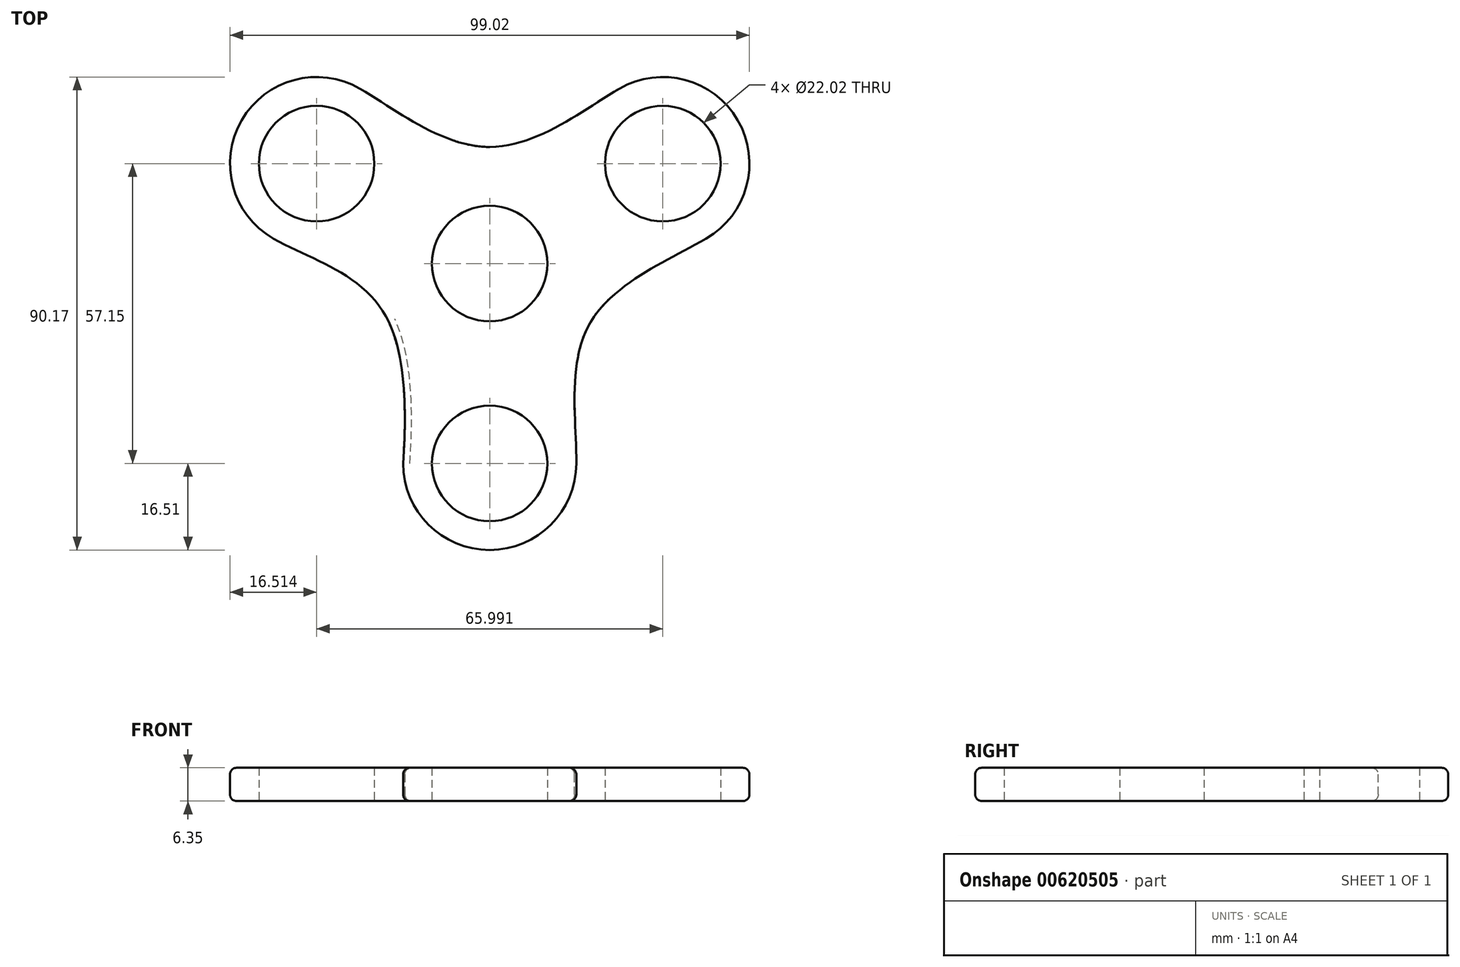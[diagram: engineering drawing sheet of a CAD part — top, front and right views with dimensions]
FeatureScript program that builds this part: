
annotation { "Feature Type Name" : "Feature", "Feature Type Description" : "" }
export const myFeature = defineFeature(function(context is Context, id is Id, definition is map)
    precondition{}
    {
        {
            var Q0;
            Q0=qCreatedBy(makeId("Top.planeOp"),FACE);
            var sketch = newSketch(context, id + "F0", { "sketchPlane" : qUnion([Q0])});
            skCircle(sketch, "E0", {"center": v(0, 0) * mm, "radius": 11.01 * mm});
            skCircle(sketch, "E1", {"center": v(-33, 19.05) * mm, "radius": 11.01 * mm});
            skCircle(sketch, "E2", {"center": v(0, -38.1) * mm, "radius": 11.01 * mm});
            skCircle(sketch, "E3", {"center": v(33, 19.05) * mm, "radius": 11.01 * mm});
            skLineSegment(sketch, "E4", {"start": v(0, 0) * mm, "end": v(-33, 19.05) * mm});
            skLineSegment(sketch, "E5", {"start": v(0, 0) * mm, "end": v(0, -38.1) * mm});
            skLineSegment(sketch, "E6", {"start": v(0, 0) * mm, "end": v(33, 19.05) * mm});
            skCircle(sketch, "E7", {"center": v(-33, 19.05) * mm, "radius": 16.51 * mm});
            skCircle(sketch, "E8", {"center": v(33, 19.05) * mm, "radius": 16.51 * mm});
            skCircle(sketch, "E9", {"center": v(0, -38.1) * mm, "radius": 16.51 * mm});
            skFitSpline(sketch, "E10", {"points": [v(-24.74, 33.35) * mm, v(0, 22.23) * mm, v(24.74, 33.35) * mm], "startDerivative": vector(38.46, -22.2) * mm, "endDerivative": vector(38.2, 22.05) * mm});
            skFitSpline(sketch, "E11", {"points": [v(41.25, 4.75) * mm, v(19.25, -11.11) * mm, v(16.51, -38.1) * mm], "startDerivative": vector(-40.53, -23.4) * mm, "endDerivative": vector(0, -52.53) * mm});
            skFitSpline(sketch, "E12", {"points": [v(-41.25, 4.75) * mm, v(-19.25, -11.11) * mm, v(-16.51, -38.1) * mm], "startDerivative": vector(40.94, -23.64) * mm, "endDerivative": vector(0, -7.4) * mm});
            skCircle(sketch, "E13", {"center": v(0, 0) * mm, "radius": 16.55 * mm});
            skLineSegment(sketch, "E14", {"start": v(0, 0) * mm, "end": v(-19.25, -11.11) * mm});
            skLineSegment(sketch, "E15", {"start": v(0, 0) * mm, "end": v(0, 22.22) * mm});
            skLineSegment(sketch, "E16", {"start": v(0, 0) * mm, "end": v(19.25, -11.11) * mm});
            skLineSegment(sketch, "E17", {"start": v(-33, 19.05) * mm, "end": v(-13.26, 53.24) * mm});
            skLineSegment(sketch, "E18", {"start": v(-13.26, 53.24) * mm, "end": v(-33, 19.05) * mm});
            skLineSegment(sketch, "E19", {"start": v(-33, 19.05) * mm, "end": v(-51.08, -12.28) * mm});
            skLineSegment(sketch, "E20", {"start": v(33, 19.05) * mm, "end": v(16.74, 47.2) * mm});
            skLineSegment(sketch, "E21", {"start": v(33, 19.05) * mm, "end": v(49.24, -9.09) * mm});
            skLineSegment(sketch, "E22", {"start": v(-26.33, -38.1) * mm, "end": v(30.94, -38.1) * mm});
            skSolve(sketch);
        }
        {
            var Q0;
            Q0 = qSketchRegion(id + "F0", true);
            var Q1;
            {var subQ0=sQuery(id+"F0.wireOp",EDGE,"E4");var subQ1=sQuery(id+"F0.wireOp",EDGE,"E0");var subQ2=makeQuery(id+"F0.imprint","INTERSECT",VERTEX,{"derivedFrom":[subQ1,subQ0]});Q1=makeQuery(id+"F0.imprint","IMPRINT",FACE,{"disambiguationData":[TD([[makeQuery(id+"F0.imprint","IMPRINT",EDGE,{"disambiguationData":[TD([[subQ2,-1.0]])],"derivedFrom":subQ1}),-1.0]])]});}
            var Q2;
            {var subQ0=sQuery(id+"F0.wireOp",EDGE,"E4");var subQ1=sQuery(id+"F0.wireOp",EDGE,"E0");var subQ2=makeQuery(id+"F0.imprint","INTERSECT",VERTEX,{"derivedFrom":[subQ1,subQ0]});Q2=makeQuery(id+"F0.imprint","IMPRINT",FACE,{"disambiguationData":[TD([[makeQuery(id+"F0.imprint","IMPRINT",EDGE,{"disambiguationData":[TD([[subQ2,1.0]])],"derivedFrom":subQ1}),-1.0]])]});}
            var Q3;
            {var subQ0=sQuery(id+"F0.wireOp",EDGE,"E6");var subQ1=sQuery(id+"F0.wireOp",EDGE,"E0");var subQ2=makeQuery(id+"F0.imprint","INTERSECT",VERTEX,{"derivedFrom":[subQ1,subQ0]});Q3=makeQuery(id+"F0.imprint","IMPRINT",FACE,{"disambiguationData":[TD([[makeQuery(id+"F0.imprint","IMPRINT",EDGE,{"disambiguationData":[TD([[subQ2,1.0]])],"derivedFrom":subQ1}),-1.0]])]});}
            var Q4;
            {var subQ0=sQuery(id+"F0.wireOp",EDGE,"E15");var subQ1=sQuery(id+"F0.wireOp",EDGE,"E0");var subQ2=makeQuery(id+"F0.imprint","INTERSECT",VERTEX,{"derivedFrom":[subQ1,subQ0]});Q4=makeQuery(id+"F0.imprint","IMPRINT",FACE,{"disambiguationData":[TD([[makeQuery(id+"F0.imprint","IMPRINT",EDGE,{"disambiguationData":[TD([[subQ2,1.0]])],"derivedFrom":subQ1}),-1.0]])]});}
            var Q5;
            {var subQ0=sQuery(id+"F0.wireOp",EDGE,"E5");var subQ1=sQuery(id+"F0.wireOp",EDGE,"E0");var subQ2=makeQuery(id+"F0.imprint","INTERSECT",VERTEX,{"derivedFrom":[subQ1,subQ0]});Q5=makeQuery(id+"F0.imprint","IMPRINT",FACE,{"disambiguationData":[TD([[makeQuery(id+"F0.imprint","IMPRINT",EDGE,{"disambiguationData":[TD([[subQ2,-1.0]])],"derivedFrom":subQ1}),-1.0]])]});}
            var Q6;
            {var subQ0=sQuery(id+"F0.wireOp",EDGE,"E14");var subQ1=sQuery(id+"F0.wireOp",EDGE,"E0");var subQ2=makeQuery(id+"F0.imprint","INTERSECT",VERTEX,{"derivedFrom":[subQ1,subQ0]});Q6=makeQuery(id+"F0.imprint","IMPRINT",FACE,{"disambiguationData":[TD([[makeQuery(id+"F0.imprint","IMPRINT",EDGE,{"disambiguationData":[TD([[subQ2,-1.0]])],"derivedFrom":subQ1}),-1.0]])]});}
            extrude(context, id + "F1", {"entities" : qUnion([Q0, Q1, Q2, Q3, Q4, Q5, Q6]), "depth" : 6.35 * mm, "offsetDistance" : 25.4 * mm});
        }
        {
            var Q0;
            Q0=makeQuery(id+"F1.opExtrude","CAP_EDGE",EDGE,{"disambiguationData":[OSD([sQuery(id+"F0.wireOp",EDGE,"E10")])],"isStart":false});
            var Q1;
            Q1=makeQuery(id+"F1.opExtrude","CAP_EDGE",EDGE,{"disambiguationData":[OSD([sQuery(id+"F0.wireOp",EDGE,"E7")])],"isStart":false});
            var Q2;
            Q2=makeQuery(id+"F1.opExtrude","CAP_EDGE",EDGE,{"disambiguationData":[OSD([sQuery(id+"F0.wireOp",EDGE,"E12")])],"isStart":false});
            var Q3;
            Q3=makeQuery(id+"F1.opExtrude","CAP_EDGE",EDGE,{"disambiguationData":[OSD([sQuery(id+"F0.wireOp",EDGE,"E9")])],"isStart":false});
            var Q4;
            Q4=makeQuery(id+"F1.opExtrude","CAP_EDGE",EDGE,{"disambiguationData":[OSD([sQuery(id+"F0.wireOp",EDGE,"E11")])],"isStart":false});
            var Q5;
            Q5=makeQuery(id+"F1.opExtrude","CAP_EDGE",EDGE,{"disambiguationData":[OSD([sQuery(id+"F0.wireOp",EDGE,"E8")])],"isStart":false});
            fillet(context, id + "F2", {"entities" : qUnion([Q0, Q1, Q2, Q3, Q4, Q5]), "radius" : 1.27 * mm, "tangentPropagation" : true, "allowEdgeOverflow" : false});
        }
        {
            var Q0;
            Q0=makeQuery(id+"F1.opExtrude","CAP_EDGE",EDGE,{"disambiguationData":[OSD([sQuery(id+"F0.wireOp",EDGE,"E12")])],"isStart":true});
            var Q1;
            Q1=makeQuery(id+"F1.opExtrude","CAP_EDGE",EDGE,{"disambiguationData":[OSD([sQuery(id+"F0.wireOp",EDGE,"E7")])],"isStart":true});
            var Q2;
            Q2=makeQuery(id+"F1.opExtrude","CAP_EDGE",EDGE,{"disambiguationData":[OSD([sQuery(id+"F0.wireOp",EDGE,"E10")])],"isStart":true});
            var Q3;
            Q3=makeQuery(id+"F1.opExtrude","CAP_EDGE",EDGE,{"disambiguationData":[OSD([sQuery(id+"F0.wireOp",EDGE,"E8")])],"isStart":true});
            var Q4;
            Q4=makeQuery(id+"F1.opExtrude","CAP_EDGE",EDGE,{"disambiguationData":[OSD([sQuery(id+"F0.wireOp",EDGE,"E11")])],"isStart":true});
            var Q5;
            Q5=makeQuery(id+"F1.opExtrude","CAP_EDGE",EDGE,{"disambiguationData":[OSD([sQuery(id+"F0.wireOp",EDGE,"E9")])],"isStart":true});
            fillet(context, id + "F3", {"entities" : qUnion([Q0, Q1, Q2, Q3, Q4, Q5]), "radius" : 1.27 * mm, "tangentPropagation" : true, "allowEdgeOverflow" : false});
        }
    });
